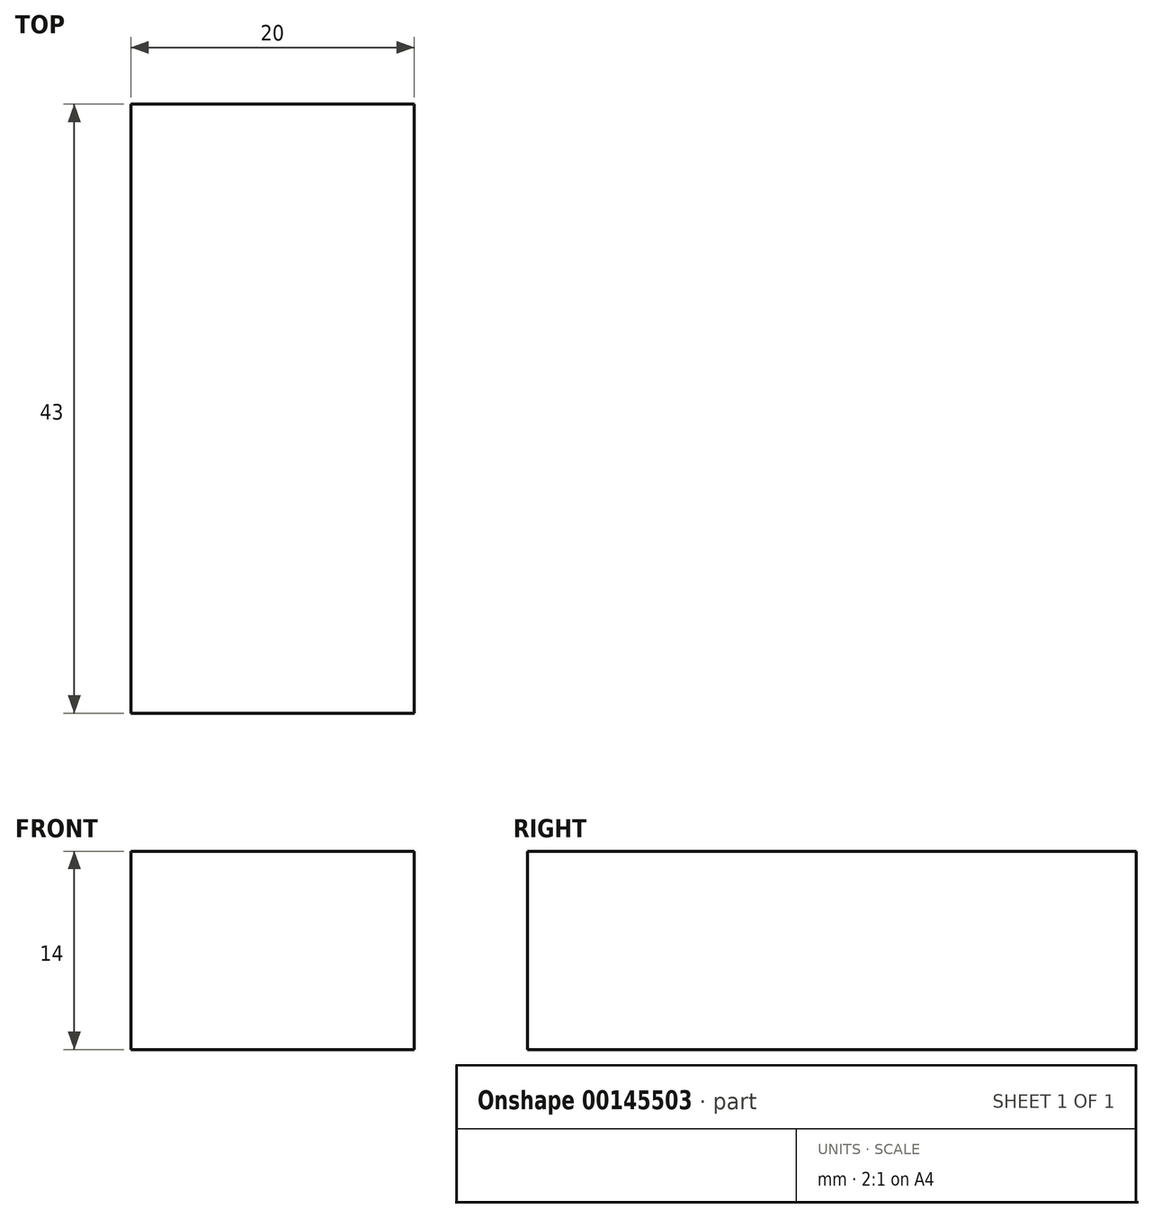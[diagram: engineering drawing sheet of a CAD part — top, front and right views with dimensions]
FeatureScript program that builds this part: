
annotation { "Feature Type Name" : "Feature", "Feature Type Description" : "" }
export const myFeature = defineFeature(function(context is Context, id is Id, definition is map)
    precondition{}
    {
        {
            var Q0;
            Q0=qCreatedBy(makeId("Front.planeOp"),FACE);
            var sketch = newSketch(context, id + "F0", { "sketchPlane" : qUnion([Q0])});
            skLineSegment(sketch, "E0.bottom", {"start": v(10, -7) * mm, "end": v(-10, -7) * mm});
            skLineSegment(sketch, "E0.top", {"start": v(10, 7) * mm, "end": v(-10, 7) * mm});
            skLineSegment(sketch, "E0.left", {"start": v(10, -7) * mm, "end": v(10, 7) * mm});
            skLineSegment(sketch, "E0.right", {"start": v(-10, -7) * mm, "end": v(-10, 7) * mm});
            skPoint(sketch, "E0.middle", {"position": v(0, 0) * mm});
            skSolve(sketch);
        }
        {
            var Q0;
            Q0 = qSketchRegion(id + "F0", true);
            extrude(context, id + "F1", {"entities" : qUnion([Q0]), "depth" : 43 * mm});
        }
    });
